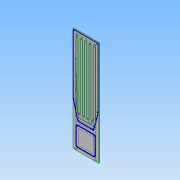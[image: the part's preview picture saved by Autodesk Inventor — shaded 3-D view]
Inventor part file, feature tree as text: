
AUTODESK INVENTOR PART (.ipt)
format: ipt  version: 2013 (Build 170138000, 138)  size: 359,424 bytes
history: native  units: in
note: dims shown in document units (in); Inventor stores cm internally (conversion verified against a paired STEP export)
features: other x13, extrude x3, hole x1, sketch x1
ambient origin geometry x8: Origin, YZ Plane, XZ Plane, XY Plane, X Axis, Y Axis, Z Axis, Center Point
bodies: Solid1 (feature_tree)
feature tree (18):
  other  "Blocks"
  extrude  "Stock Extrusion"  Depth=96.0in
  extrude  "LED Pocket Extrusion"  TaperAngle=0.0deg  [1 undecoded]
  other  "Side profile reference"
  hole  "Hole1"  [1 undecoded]
  extrude  "Through Panel Extrusion5"  Depth=1.0in
  other  "Exclaim Point"
  sketch  "Sketch10"  dims[d1=23.8125in d2=96.0in d3=0.0in d4=60.0in d6=1.0in d7=2.9062in d9=0.24in d10=0.24in d18=2.5in d19=4.75in d20=96.0in d21=21.3125in d22=60.0in d23=2.0in d25=0.24in d26=0.24in d29=2.0in d32=2.5in d33=1.74in d38=31.25in d41=60.0in d42=2.0in d43=0.24in d44=0.24in d45=2.0in d47=2.0in d49=60.0in d50=2.0in d51=1.0in d52=0.24in d53=0.24in d63=0.5in d64=0.0in d73=0.55in d74=0.47in d75=0.5in d76=0.58in d80=0.48in d88=0.25in d89=4.75in d90=2.5in d91=0.75in d92=1.0in d93=0.1in d94=0.25in d95=0.5in d96=0.25in d97=0.205in d98=0.0in d99=0.5in d100=0.75in d102=1.375in d105=0.3125in d109=1.3in d110=1.375in d111=1.375in d112=0.75in d113=2.125in d114=2.125in d115=1.375in d116=1.375in d117=0.75in d119=0.3125in d120=0.75in d121=0.75in d122=0.25in d123=0.5635in d124=1.0in d125=0.8108in d126=2.875in d127=1.75in d129=2.25in d130=0.1875in d131=4.0in d132=0.0in d133=0.0in d138=2.5in d139=0.41in d140=0.41in d141=0.41in d142=165.0deg d144=2.5in d145=2.5in d146=2.5in d147=2.5in d148=0.66in d149=0.66in d150=0.66in d151=3.5in d152=16.0in d154=0.75in d155=0.75in d156=0.16in d157=0.32in d158=0.75in d159=0.16in d160=0.32in d161=2.5in d162=1.25in d163=2.5in d164=8.0in d165=2.5in d166=15.0in d167=0.48in d168=1.0in]
  other  "Stock"
  other  "LEDPocket"
  other  "TwoLineColumn"
  other  "TwoLineColumnEnd"
  other  "15mm Neon profile"
  other  "U Bolt hole and bore"
  other  "U-Bolt holes"
  other  "WeatherProof panel"
  other  "15mm Neon profile:1"
  other  "15mm Neon profile:2"
note: 2 required parameter values undecoded (feature->parameter linkage not recoverable at this tier; creation-order binding heuristic only, values carry confidence <= 0.55)
